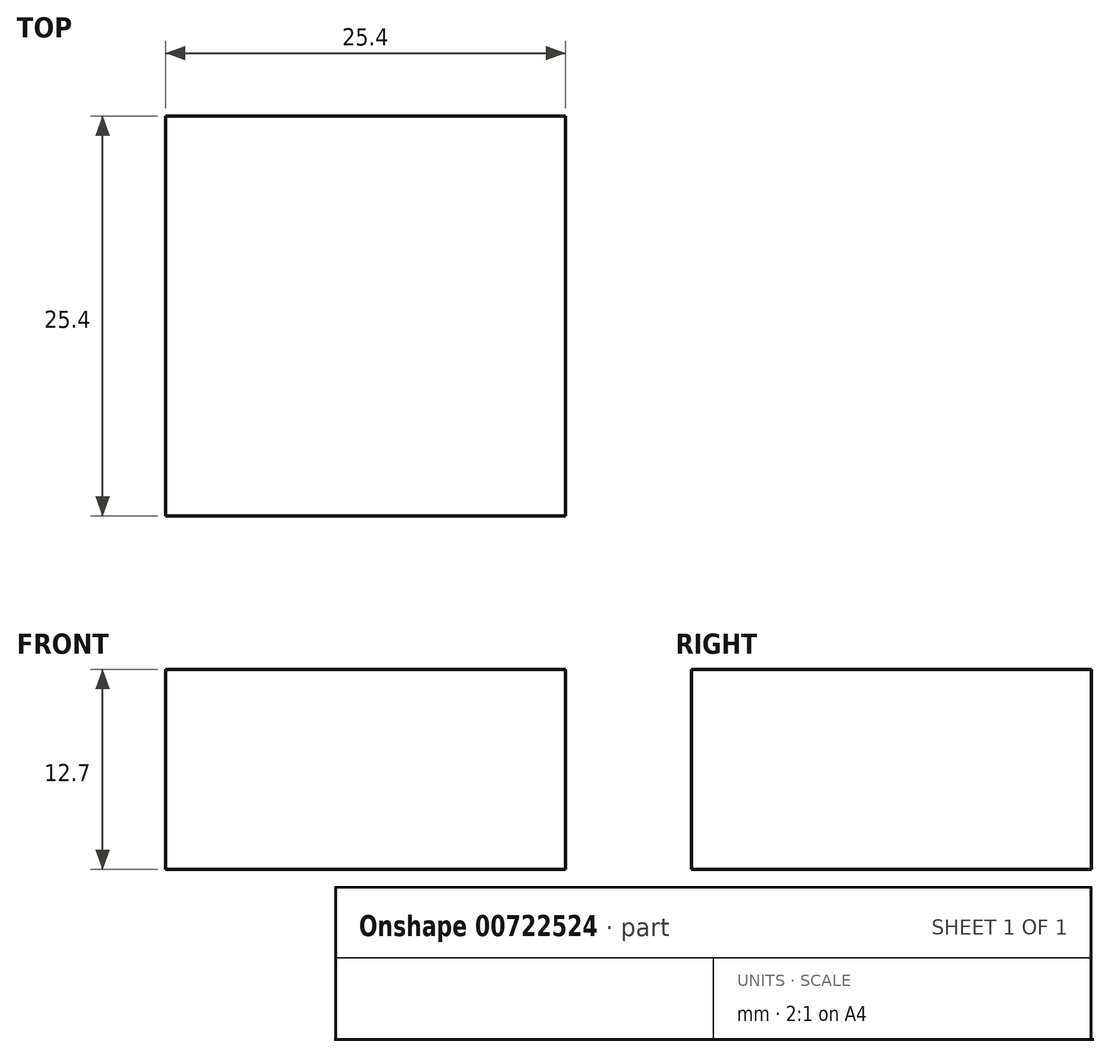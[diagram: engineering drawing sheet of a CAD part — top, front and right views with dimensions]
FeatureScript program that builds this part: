
annotation { "Feature Type Name" : "Feature", "Feature Type Description" : "" }
export const myFeature = defineFeature(function(context is Context, id is Id, definition is map)
    precondition{}
    {
        {
            var Q0;
            Q0=qCreatedBy(makeId("Top.planeOp"),FACE);
            var sketch = newSketch(context, id + "F0", { "sketchPlane" : qUnion([Q0])});
            skLineSegment(sketch, "E0.bottom", {"start": v(0, 0) * mm, "end": v(25.4, 0) * mm});
            skLineSegment(sketch, "E0.top", {"start": v(0, 25.4) * mm, "end": v(25.4, 25.4) * mm});
            skLineSegment(sketch, "E0.left", {"start": v(0, 0) * mm, "end": v(0, 25.4) * mm});
            skLineSegment(sketch, "E0.right", {"start": v(25.4, 0) * mm, "end": v(25.4, 25.4) * mm});
            skSolve(sketch);
        }
        {
            var Q0;
            Q0 = qSketchRegion(id + "F0", true);
            extrude(context, id + "F1", {"entities" : qUnion([Q0]), "depth" : 12.7 * mm, "offsetDistance" : 25.4 * mm});
        }
    });
